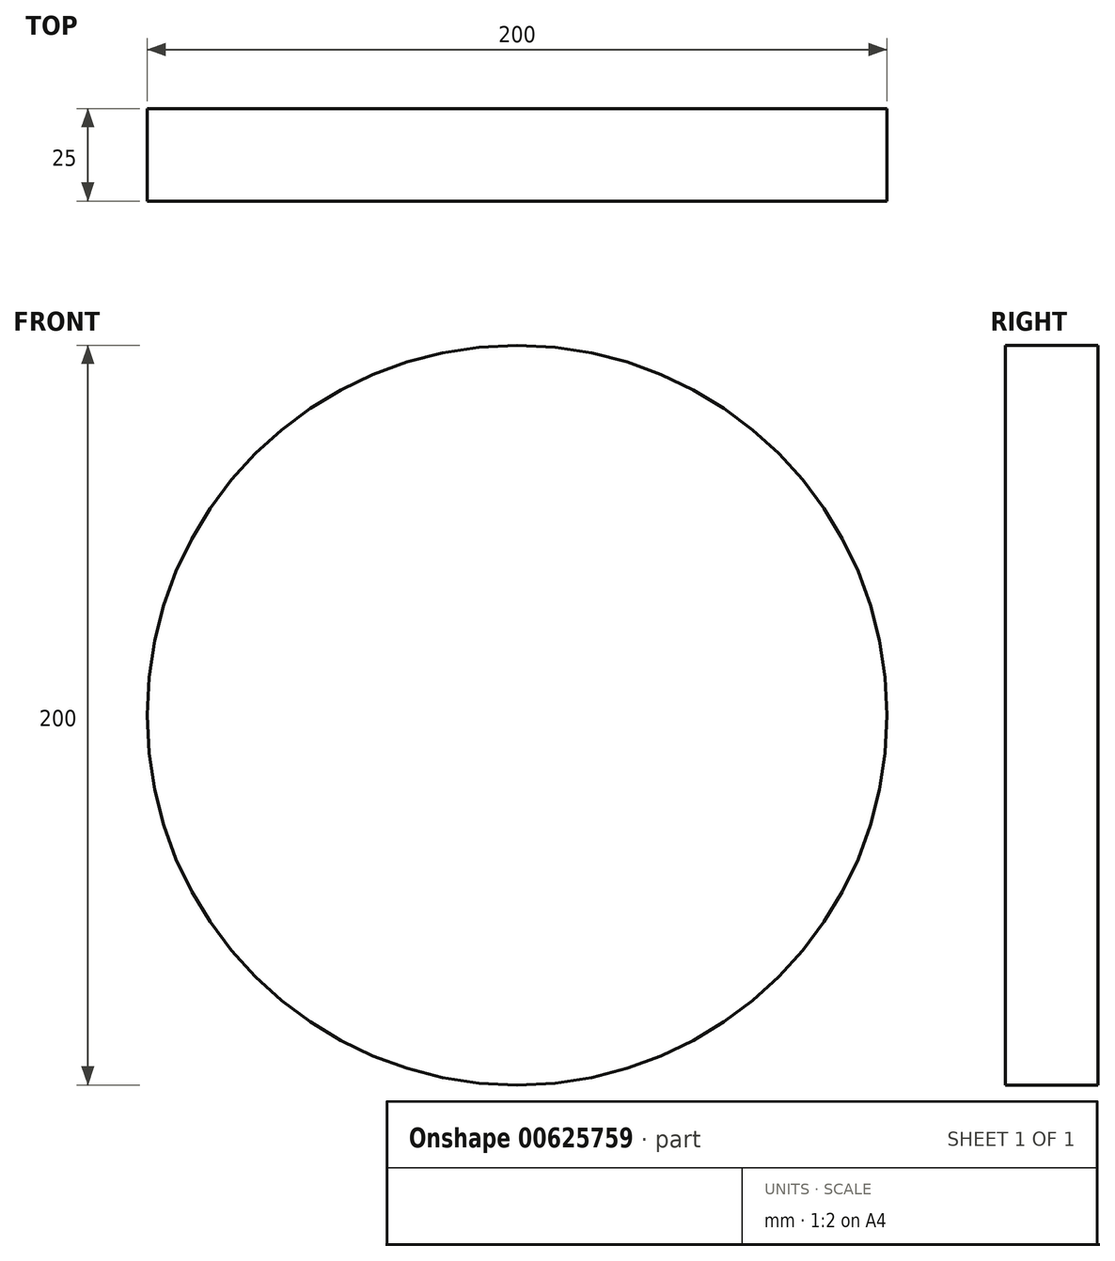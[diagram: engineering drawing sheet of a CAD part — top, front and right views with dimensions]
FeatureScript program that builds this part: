
annotation { "Feature Type Name" : "Feature", "Feature Type Description" : "" }
export const myFeature = defineFeature(function(context is Context, id is Id, definition is map)
    precondition{}
    {
        {
            var Q0;
            Q0=qCreatedBy(makeId("Front.planeOp"),FACE);
            var sketch = newSketch(context, id + "F0", { "sketchPlane" : qUnion([Q0])});
            skCircle(sketch, "E0", {"center": v(0, 0) * mm, "radius": 100 * mm});
            skCircle(sketch, "E1", {"center": v(0, 0) * mm, "radius": 120 * mm, "construction": true});
            skSolve(sketch);
        }
        {
            var Q0;
            Q0=makeQuery(id+"F0.imprint","IMPRINT",FACE,{"disambiguationData":[TD([[makeQuery(id+"F0.imprint","IMPRINT",EDGE,{"derivedFrom":sQuery(id+"F0.wireOp",EDGE,"E0")}),1.0]])]});
            extrude(context, id + "F1", {"entities" : qUnion([Q0]), "depth" : 25 * mm, "offsetDistance" : 25 * mm});
        }
    });
